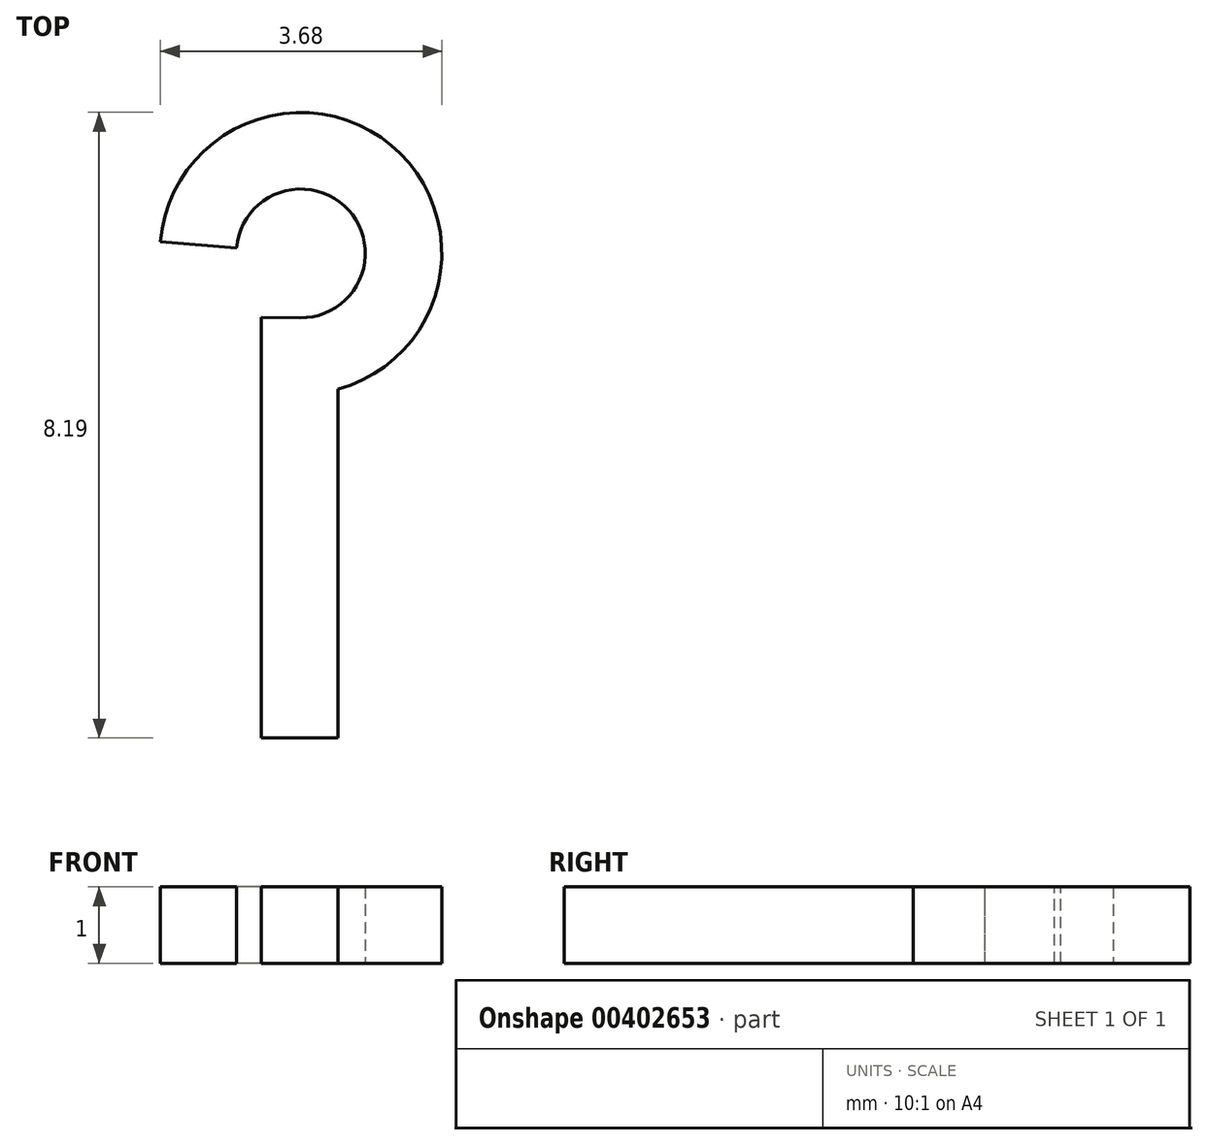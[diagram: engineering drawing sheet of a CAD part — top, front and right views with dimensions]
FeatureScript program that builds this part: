
annotation { "Feature Type Name" : "Feature", "Feature Type Description" : "" }
export const myFeature = defineFeature(function(context is Context, id is Id, definition is map)
    precondition{}
    {
        {
            var Q0;
            Q0=qCreatedBy(makeId("Front.planeOp"),FACE);
            var sketch = newSketch(context, id + "F0", { "sketchPlane" : qUnion([Q0])});
            skLineSegment(sketch, "E0.bottom", {"start": v(0.5, -0.5) * mm, "end": v(-0.5, -0.5) * mm});
            skLineSegment(sketch, "E0.top", {"start": v(0.5, 0.5) * mm, "end": v(-0.5, 0.5) * mm});
            skLineSegment(sketch, "E0.left", {"start": v(0.5, -0.5) * mm, "end": v(0.5, 0.5) * mm});
            skLineSegment(sketch, "E0.right", {"start": v(-0.5, -0.5) * mm, "end": v(-0.5, 0.5) * mm});
            skPoint(sketch, "E0.middle", {"position": v(0, 0) * mm});
            skSolve(sketch);
        }
        {
            var Q0;
            Q0=qCreatedBy(makeId("Top.planeOp"),FACE);
            var sketch = newSketch(context, id + "F1", { "sketchPlane" : qUnion([Q0])});
            skLineSegment(sketch, "E1", {"start": v(0, 0) * mm, "end": v(0, 5) * mm});
            skArc(sketch, "E2", {"start": v(0, 5) * mm, "mid": v(1, 7.25) * mm, "end": v(-1.32, 6.46) * mm});
            skSolve(sketch);
        }
        {
            var Q0;
            Q0=makeQuery(id+"F0.imprint","IMPRINT",FACE,{"disambiguationData":[TD([[makeQuery(id+"F0.imprint","IMPRINT",EDGE,{"derivedFrom":sQuery(id+"F0.wireOp",EDGE,"E0.bottom")}),-1.0]])]});
            var Q1;
            Q1=sQuery(id+"F1.wireOp",EDGE,"E2");
            var Q2;
            Q2=sQuery(id+"F1.wireOp",EDGE,"E1");
            sweep(context, id + "F2", {"profiles" : qUnion([Q0]), "path" : qUnion([Q1, Q2])});
        }
    });
